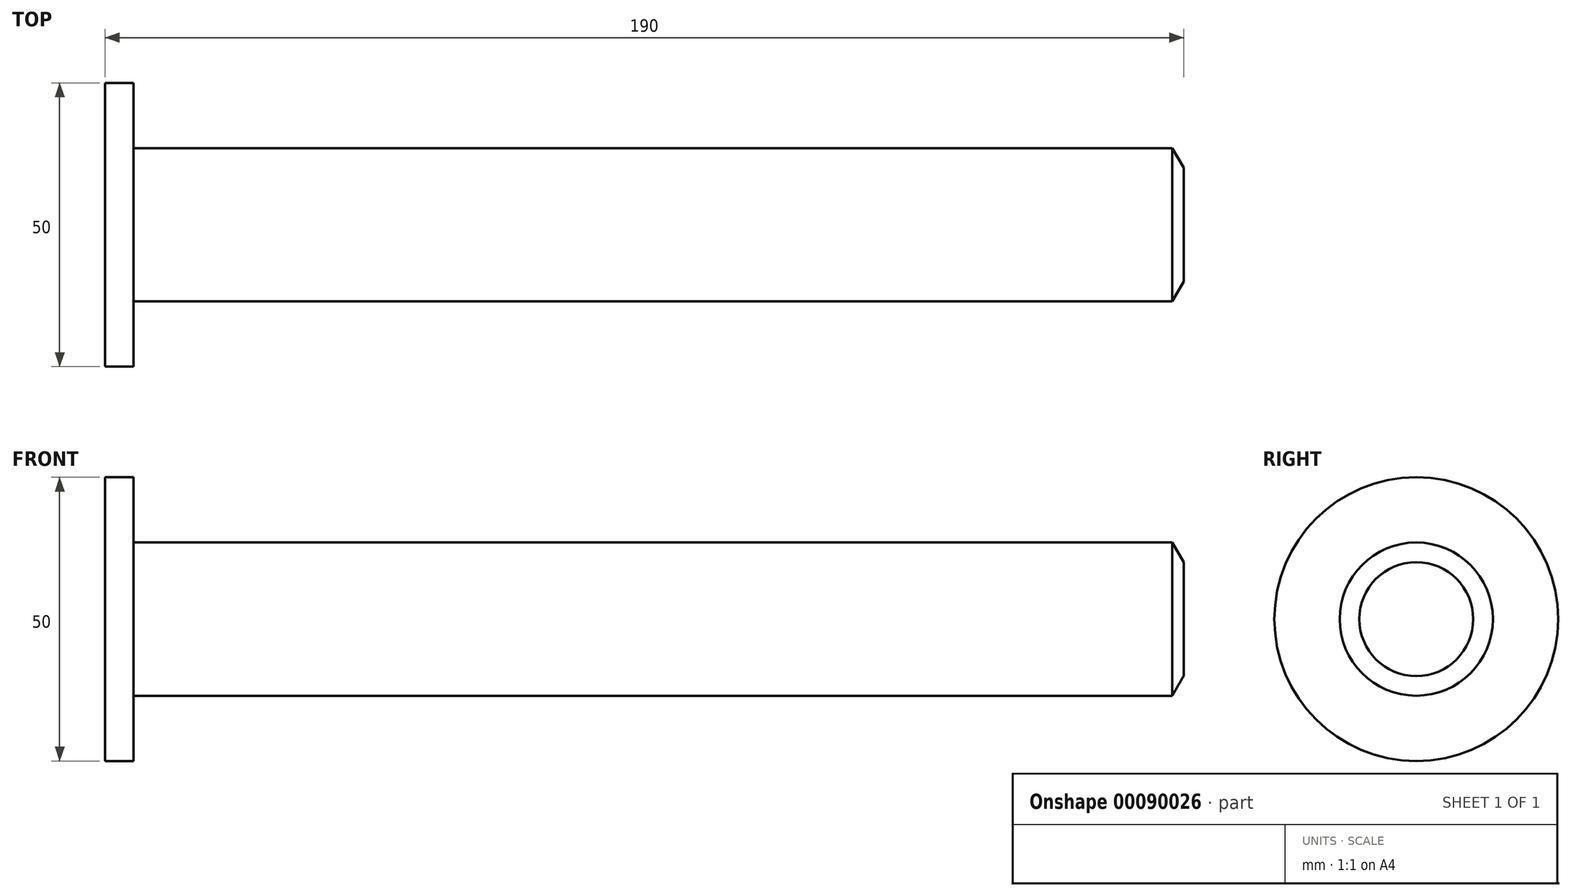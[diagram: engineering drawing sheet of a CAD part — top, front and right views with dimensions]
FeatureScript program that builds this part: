
annotation { "Feature Type Name" : "Feature", "Feature Type Description" : "" }
export const myFeature = defineFeature(function(context is Context, id is Id, definition is map)
    precondition{}
    {
        {
            var Q0;
            Q0=qCreatedBy(makeId("Right.planeOp"),FACE);
            var sketch = newSketch(context, id + "F0", { "sketchPlane" : qUnion([Q0])});
            skCircle(sketch, "E0", {"center": v(0, 0) * mm, "radius": 25 * mm});
            skCircle(sketch, "E1", {"center": v(0, 0) * mm, "radius": 13.5 * mm});
            skSolve(sketch);
        }
        {
            var Q0;
            Q0=makeQuery(id+"F0.imprint","IMPRINT",FACE,{"disambiguationData":[TD([[makeQuery(id+"F0.imprint","IMPRINT",EDGE,{"derivedFrom":sQuery(id+"F0.wireOp",EDGE,"E1")}),1.0]])]});
            extrude(context, id + "F1", {"entities" : qUnion([Q0]), "depth" : 190 * mm});
        }
        {
            var Q0;
            Q0=makeQuery(id+"F0.imprint","IMPRINT",FACE,{"disambiguationData":[TD([[makeQuery(id+"F0.imprint","IMPRINT",EDGE,{"derivedFrom":sQuery(id+"F0.wireOp",EDGE,"E0")}),1.0]])]});
            extrude(context, id + "F2", {"entities" : qUnion([Q0]), "operationType" : NewBodyOperationType.ADD, "depth" : 5 * mm});
        }
        {
            var Q0;
            Q0=makeQuery(id+"F1.opExtrude","CAP_EDGE",EDGE,{"disambiguationData":[OSD([sQuery(id+"F0.wireOp",EDGE,"E1")])],"isStart":false});
            chamfer(context, id + "F3", {"entities" : qUnion([Q0]), "chamferType" : ChamferType.OFFSET_ANGLE, "width" : 2 * mm, "oppositeDirection" : false, "angle" : 60 * degree, "tangentPropagation" : true});
        }
    });
